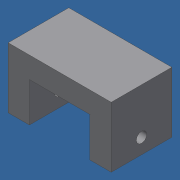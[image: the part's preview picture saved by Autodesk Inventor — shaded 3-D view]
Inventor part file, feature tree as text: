
AUTODESK INVENTOR PART (.ipt)
format: ipt  version: 2021 (Build 250183000, 183)  size: 95,232 bytes
history: native  units: mm
features: extrude x2, sketch x2
ambient origin geometry x8: Origin, YZ Plane, XZ Plane, XY Plane, X Axis, Y Axis, Z Axis, Center Point
bodies: Solid1 (feature_tree)
feature tree (4):
  extrude  "Extrusion1"  Depth=7.0mm
  extrude  "Extrusion2"  Depth=7.0mm
  sketch  "Sketch1"  dims[d0=34.0mm d1=7.0mm]
  sketch  "Sketch2"  dims[d2=7.0mm d3=7.0mm d4=13.0mm d5=20.0mm d6=0.0mm d7=5.0mm d8=10.0mm d9=5.0mm d10=60.0mm d11=10.0mm d12=0.0mm d13=0.0mm]
